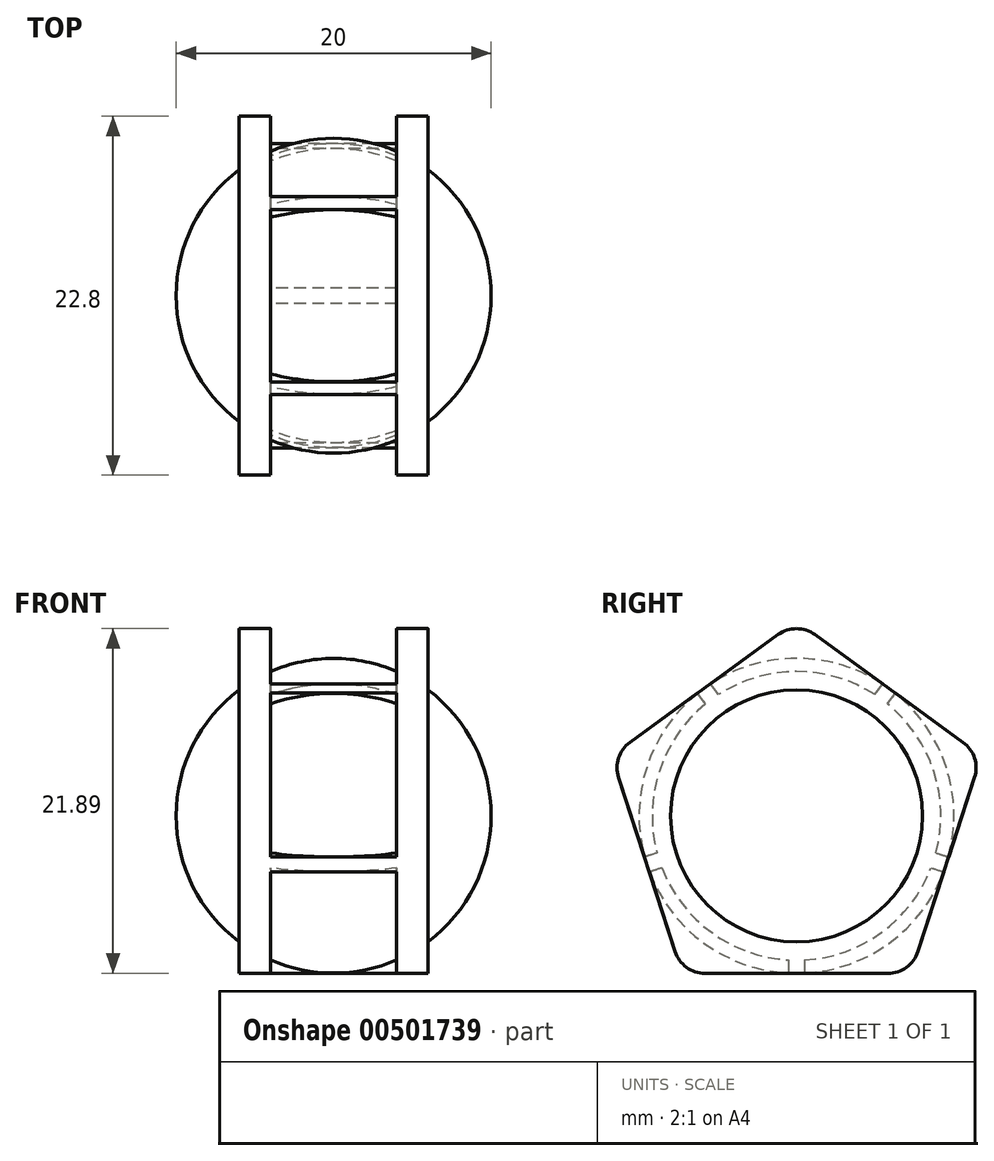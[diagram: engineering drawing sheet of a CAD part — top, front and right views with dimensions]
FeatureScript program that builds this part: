
annotation { "Feature Type Name" : "Feature", "Feature Type Description" : "" }
export const myFeature = defineFeature(function(context is Context, id is Id, definition is map)
    precondition{}
    {
        {
            var Q0;
            Q0=qCreatedBy(makeId("Right.planeOp"),FACE);
            var sketch = newSketch(context, id + "F0", { "sketchPlane" : qUnion([Q0])});
            skArc(sketch, "E0", {"start": v(0, 10) * mm, "mid": v(-10, 0) * mm, "end": v(0, -10) * mm});
            skLineSegment(sketch, "E1", {"start": v(0, 10) * mm, "end": v(0, -10) * mm});
            skSolve(sketch);
        }
        {
            var Q0;
            Q0 = qSketchRegion(id + "F0", true);
            var Q1;
            Q1=sQuery(id+"F0.wireOp",EDGE,"E1");
            revolve(context, id + "F1", {"entities" : qUnion([Q0]), "axis" : qUnion([Q1]), "revolveType" : RevolveType.FULL});
        }
        {
            var Q0;
            Q0=qCreatedBy(makeId("Right.planeOp"),FACE);
            cPlane(context, id + "F2", {"entities" : qUnion([Q0]), "cplaneType" : CPlaneType.OFFSET, "offset" : 5 * mm, "width" : 150 * mm, "height" : 150 * mm});
        }
        {
            var Q0;
            Q0=qCreatedBy(id+"F2.planeOp",FACE);
            var sketch = newSketch(context, id + "F3", { "sketchPlane" : qUnion([Q0])});
            skLineSegment(sketch, "E2.0", {"start": v(0, 10) * mm, "end": v(0, -10) * mm, "construction": true});
            skCircle(sketch, "E3.cCircle", {"center": v(0, 0) * mm, "radius": 10 * mm, "construction": true});
            skLineSegment(sketch, "E3.0", {"start": v(7.27, -10) * mm, "end": v(-7.27, -10) * mm});
            skLineSegment(sketch, "E3.1", {"start": v(-7.27, -10) * mm, "end": v(-11.76, 3.82) * mm});
            skLineSegment(sketch, "E3.2", {"start": v(-11.76, 3.82) * mm, "end": v(0, 12.36) * mm});
            skLineSegment(sketch, "E3.3", {"start": v(0, 12.36) * mm, "end": v(11.76, 3.82) * mm});
            skLineSegment(sketch, "E3.4", {"start": v(11.76, 3.82) * mm, "end": v(7.27, -10) * mm});
            skPoint(sketch, "E3.0.midPoint", {"position": v(0, -10) * mm});
            skSolve(sketch);
        }
        {
            var Q0;
            Q0=makeQuery(id+"F3.imprint","IMPRINT",FACE,{"disambiguationData":[TD([[makeQuery(id+"F3.imprint","IMPRINT",EDGE,{"derivedFrom":sQuery(id+"F3.wireOp",EDGE,"E3.0")}),-1.0]])]});
            extrude(context, id + "F4", {"entities" : qUnion([Q0]), "operationType" : NewBodyOperationType.ADD, "endBound" : BoundingType.SYMMETRIC, "depth" : 2 * mm});
        }
        {
            var Q0;
            Q0=qCreatedBy(makeId("Right.planeOp"),FACE);
            cPlane(context, id + "F5", {"entities" : qUnion([Q0]), "cplaneType" : CPlaneType.OFFSET, "offset" : 5 * mm, "oppositeDirection" : true, "width" : 150 * mm, "height" : 150 * mm});
        }
        {
            var Q0;
            Q0=qCreatedBy(id+"F5.planeOp",FACE);
            var sketch = newSketch(context, id + "F6", { "sketchPlane" : qUnion([Q0])});
            skLineSegment(sketch, "E4.0", {"start": v(0, 10) * mm, "end": v(0, -10) * mm, "construction": true});
            skCircle(sketch, "E5.cCircle", {"center": v(0, 0) * mm, "radius": 10 * mm, "construction": true});
            skLineSegment(sketch, "E5.0", {"start": v(7.27, -10) * mm, "end": v(-7.27, -10) * mm});
            skLineSegment(sketch, "E5.1", {"start": v(-7.27, -10) * mm, "end": v(-11.76, 3.82) * mm});
            skLineSegment(sketch, "E5.2", {"start": v(-11.76, 3.82) * mm, "end": v(0, 12.36) * mm});
            skLineSegment(sketch, "E5.3", {"start": v(0, 12.36) * mm, "end": v(11.76, 3.82) * mm});
            skLineSegment(sketch, "E5.4", {"start": v(11.76, 3.82) * mm, "end": v(7.27, -10) * mm});
            skPoint(sketch, "E5.0.midPoint", {"position": v(0, -10) * mm});
            skSolve(sketch);
        }
        {
            var Q0;
            Q0 = qSketchRegion(id + "F6", true);
            extrude(context, id + "F7", {"entities" : qUnion([Q0]), "operationType" : NewBodyOperationType.ADD, "endBound" : BoundingType.SYMMETRIC, "depth" : 2 * mm});
        }
        {
            var Q0;
            Q0=makeQuery(id+"F7.opExtrude","SWEPT_EDGE",EDGE,{"disambiguationData":[OSD([sQuery(id+"F6.wireOp",EDGE,"E5.1"),sQuery(id+"F6.wireOp",EDGE,"E5.2")])]});
            var Q1;
            Q1=makeQuery(id+"F7.opExtrude","SWEPT_EDGE",EDGE,{"disambiguationData":[OSD([sQuery(id+"F6.wireOp",EDGE,"E5.2"),sQuery(id+"F6.wireOp",EDGE,"E5.3")])]});
            var Q2;
            Q2=makeQuery(id+"F4.opExtrude","SWEPT_EDGE",EDGE,{"disambiguationData":[OSD([sQuery(id+"F3.wireOp",EDGE,"E3.2"),sQuery(id+"F3.wireOp",EDGE,"E3.3")])]});
            var Q3;
            Q3=makeQuery(id+"F4.opExtrude","SWEPT_EDGE",EDGE,{"disambiguationData":[OSD([sQuery(id+"F3.wireOp",EDGE,"E3.1"),sQuery(id+"F3.wireOp",EDGE,"E3.2")])]});
            var Q4;
            Q4=makeQuery(id+"F7.opExtrude","SWEPT_EDGE",EDGE,{"disambiguationData":[OSD([sQuery(id+"F6.wireOp",EDGE,"E5.0"),sQuery(id+"F6.wireOp",EDGE,"E5.1")])]});
            var Q5;
            Q5=makeQuery(id+"F4.opExtrude","SWEPT_EDGE",EDGE,{"disambiguationData":[OSD([sQuery(id+"F3.wireOp",EDGE,"E3.0"),sQuery(id+"F3.wireOp",EDGE,"E3.1")])]});
            var Q6;
            Q6=makeQuery(id+"F4.opExtrude","SWEPT_EDGE",EDGE,{"disambiguationData":[OSD([sQuery(id+"F3.wireOp",EDGE,"E3.3"),sQuery(id+"F3.wireOp",EDGE,"E3.4")])]});
            var Q7;
            Q7=makeQuery(id+"F7.opExtrude","SWEPT_EDGE",EDGE,{"disambiguationData":[OSD([sQuery(id+"F6.wireOp",EDGE,"E5.3"),sQuery(id+"F6.wireOp",EDGE,"E5.4")])]});
            var Q8;
            Q8=makeQuery(id+"F4.opExtrude","SWEPT_EDGE",EDGE,{"disambiguationData":[OSD([sQuery(id+"F3.wireOp",EDGE,"E3.0"),sQuery(id+"F3.wireOp",EDGE,"E3.4")])]});
            var Q9;
            Q9=makeQuery(id+"F7.opExtrude","SWEPT_EDGE",EDGE,{"disambiguationData":[OSD([sQuery(id+"F6.wireOp",EDGE,"E5.0"),sQuery(id+"F6.wireOp",EDGE,"E5.4")])]});
            fillet(context, id + "F8", {"entities" : qUnion([Q0, Q1, Q2, Q3, Q4, Q5, Q6, Q7, Q8, Q9]), "radius" : 2 * mm, "tangentPropagation" : true, "allowEdgeOverflow" : false});
        }
        {
            var Q0;
            Q0=makeQuery(id+"F7.opExtrude","CAP_FACE",FACE,{"disambiguationData":[OSD([sQuery(id+"F6.wireOp",EDGE,"E5.0"),sQuery(id+"F6.wireOp",EDGE,"E5.1"),sQuery(id+"F6.wireOp",EDGE,"E5.2"),sQuery(id+"F6.wireOp",EDGE,"E5.3"),sQuery(id+"F6.wireOp",EDGE,"E5.4")])],"isStart":false});
            var sketch = newSketch(context, id + "F9", { "sketchPlane" : qUnion([Q0])});
            skCircle(sketch, "E6.0", {"center": v(0, 0) * mm, "radius": 9.17 * mm, "construction": true});
            skLineSegment(sketch, "E7.0", {"start": v(-10.58, 4.67) * mm, "end": v(-1.18, 11.5) * mm, "construction": true});
            skLineSegment(sketch, "E8.0", {"start": v(-7.71, -8.62) * mm, "end": v(-11.3, 2.44) * mm, "construction": true});
            skLineSegment(sketch, "E9.0", {"start": v(1.18, 11.5) * mm, "end": v(10.58, 4.67) * mm, "construction": true});
            skLineSegment(sketch, "E10.0", {"start": v(11.3, 2.44) * mm, "end": v(7.71, -8.62) * mm, "construction": true});
            skLineSegment(sketch, "E11.0", {"start": v(5.81, -10) * mm, "end": v(-5.81, -10) * mm, "construction": true});
            skLineSegment(sketch, "E12.0", {"start": v(-4.97, 7.7) * mm, "end": v(-5.47, 8.38) * mm});
            skLineSegment(sketch, "E13.0", {"start": v(-5.78, 7.1) * mm, "end": v(-6.28, 7.8) * mm});
            skLineSegment(sketch, "E14.1.0", {"start": v(-8.86, -2.35) * mm, "end": v(-9.67, -2.61) * mm});
            skLineSegment(sketch, "E14.1.1", {"start": v(-8.55, -3.3) * mm, "end": v(-9.36, -3.57) * mm});
            skLineSegment(sketch, "E14.2.0", {"start": v(-0.5, -9.15) * mm, "end": v(-0.5, -10) * mm});
            skLineSegment(sketch, "E14.2.1", {"start": v(0.5, -9.15) * mm, "end": v(0.5, -10) * mm});
            skLineSegment(sketch, "E15.3.3.0", {"start": v(8.86, -2.35) * mm, "end": v(9.67, -2.61) * mm});
            skLineSegment(sketch, "E15.4.3.0", {"start": v(8.55, -3.3) * mm, "end": v(9.36, -3.57) * mm});
            skLineSegment(sketch, "E15.3.4.0", {"start": v(4.97, 7.7) * mm, "end": v(5.47, 8.38) * mm});
            skLineSegment(sketch, "E15.4.4.0", {"start": v(5.78, 7.1) * mm, "end": v(6.28, 7.8) * mm});
            skSolve(sketch);
        }
        {
            var Q0;
            {var subQ0=sQuery(id+"F9.wireOp",EDGE,"E12.0");Q0=makeQuery(id+"F9.imprint","IMPRINT",FACE,{"disambiguationData":[TD([[makeQuery(id+"F9.imprint","IMPRINT",EDGE,{"derivedFrom":subQ0}),1.0]])]});}
            var Q1;
            {var subQ0=sQuery(id+"F9.wireOp",EDGE,"E15.3.4.0");Q1=makeQuery(id+"F9.imprint","IMPRINT",FACE,{"disambiguationData":[TD([[makeQuery(id+"F9.imprint","IMPRINT",EDGE,{"derivedFrom":subQ0}),-1.0]])]});}
            var Q2;
            {var subQ0=sQuery(id+"F9.wireOp",EDGE,"E15.3.3.0");Q2=makeQuery(id+"F9.imprint","IMPRINT",FACE,{"disambiguationData":[TD([[makeQuery(id+"F9.imprint","IMPRINT",EDGE,{"derivedFrom":subQ0}),-1.0]])]});}
            var Q3;
            {var subQ0=sQuery(id+"F9.wireOp",EDGE,"E14.2.0");Q3=makeQuery(id+"F9.imprint","IMPRINT",FACE,{"disambiguationData":[TD([[makeQuery(id+"F9.imprint","IMPRINT",EDGE,{"derivedFrom":subQ0}),1.0]])]});}
            var Q4;
            {var subQ0=sQuery(id+"F9.wireOp",EDGE,"E14.1.0");Q4=makeQuery(id+"F9.imprint","IMPRINT",FACE,{"disambiguationData":[TD([[makeQuery(id+"F9.imprint","IMPRINT",EDGE,{"derivedFrom":subQ0}),1.0]])]});}
            extrude(context, id + "F10", {"entities" : qUnion([Q0, Q1, Q2, Q3, Q4]), "operationType" : NewBodyOperationType.ADD, "depth" : 8 * mm});
        }
    });
